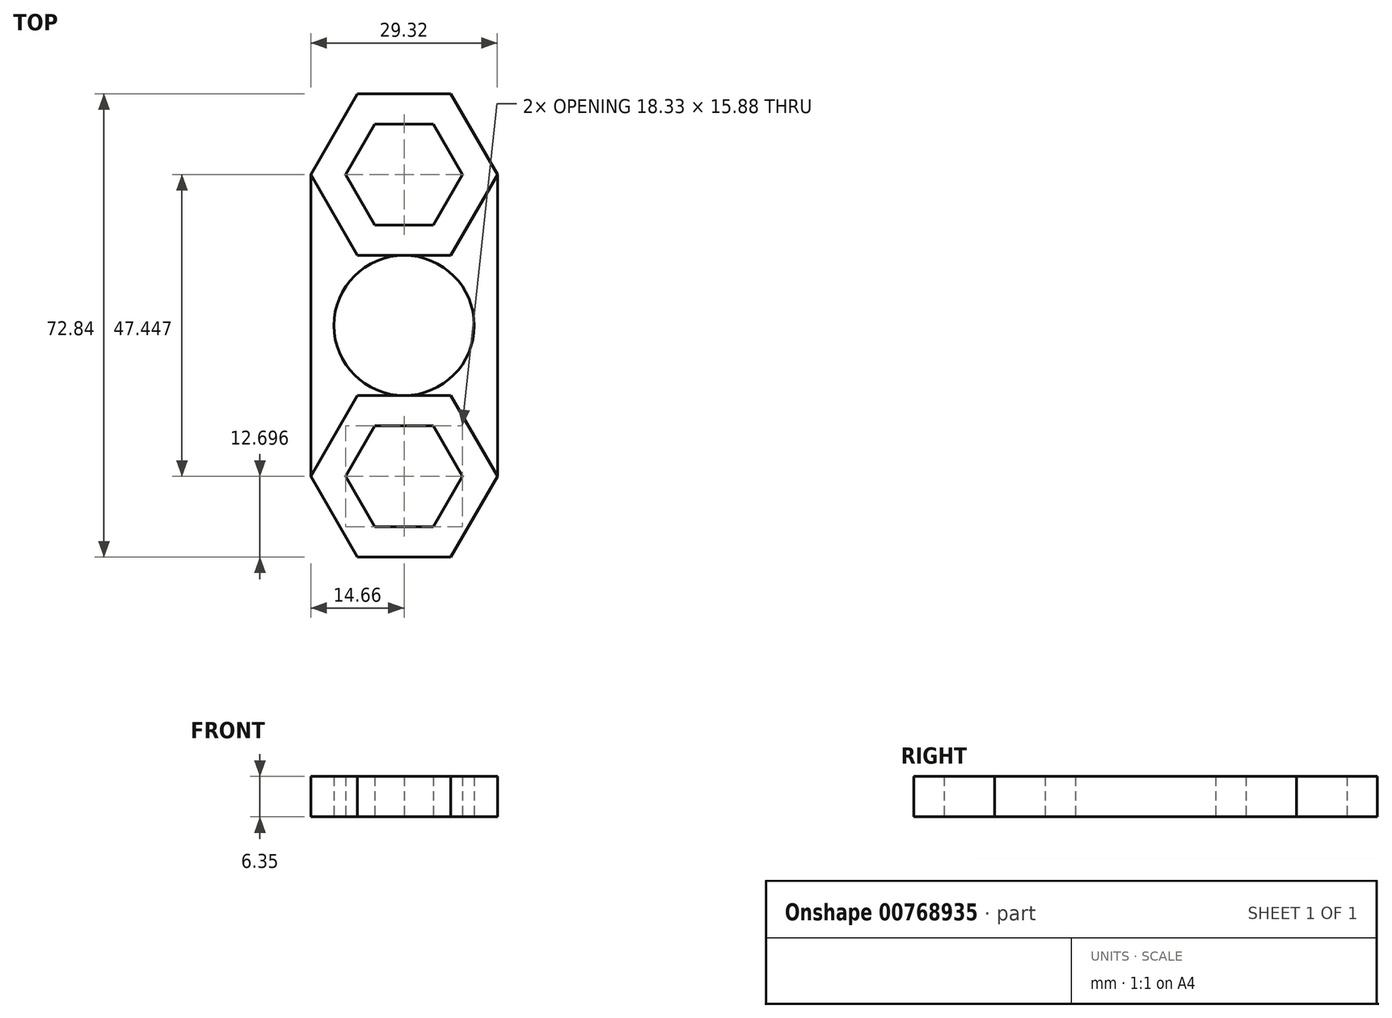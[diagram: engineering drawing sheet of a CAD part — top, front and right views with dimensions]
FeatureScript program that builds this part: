
annotation { "Feature Type Name" : "Feature", "Feature Type Description" : "" }
export const myFeature = defineFeature(function(context is Context, id is Id, definition is map)
    precondition{}
    {
        {
            var Q0;
            Q0=qCreatedBy(makeId("Top.planeOp"),FACE);
            var sketch = newSketch(context, id + "F0", { "sketchPlane" : qUnion([Q0])});
            skCircle(sketch, "E0", {"center": v(0, 0) * mm, "radius": 11.02 * mm});
            skCircle(sketch, "E1.cCircle", {"center": v(0, 23.72) * mm, "radius": 7.94 * mm, "construction": true});
            skLineSegment(sketch, "E1.0", {"start": v(4.58, 15.79) * mm, "end": v(-4.58, 15.79) * mm});
            skLineSegment(sketch, "E1.1", {"start": v(-4.58, 15.79) * mm, "end": v(-9.17, 23.72) * mm});
            skLineSegment(sketch, "E1.2", {"start": v(-9.17, 23.72) * mm, "end": v(-4.58, 31.66) * mm});
            skLineSegment(sketch, "E1.3", {"start": v(-4.58, 31.66) * mm, "end": v(4.58, 31.66) * mm});
            skLineSegment(sketch, "E1.4", {"start": v(4.58, 31.66) * mm, "end": v(9.17, 23.72) * mm});
            skLineSegment(sketch, "E1.5", {"start": v(9.17, 23.72) * mm, "end": v(4.58, 15.79) * mm});
            skPoint(sketch, "E1.0.midPoint", {"position": v(0, 15.79) * mm});
            skCircle(sketch, "E2.cCircle", {"center": v(0, 23.72) * mm, "radius": 12.7 * mm, "construction": true});
            skLineSegment(sketch, "E2.0", {"start": v(7.33, 11.02) * mm, "end": v(-7.33, 11.02) * mm});
            skLineSegment(sketch, "E2.1", {"start": v(-7.33, 11.02) * mm, "end": v(-14.66, 23.72) * mm});
            skLineSegment(sketch, "E2.2", {"start": v(-14.66, 23.72) * mm, "end": v(-7.33, 36.42) * mm});
            skLineSegment(sketch, "E2.3", {"start": v(-7.33, 36.42) * mm, "end": v(7.33, 36.42) * mm});
            skLineSegment(sketch, "E2.4", {"start": v(7.33, 36.42) * mm, "end": v(14.66, 23.72) * mm});
            skLineSegment(sketch, "E2.5", {"start": v(14.66, 23.72) * mm, "end": v(7.33, 11.02) * mm});
            skPoint(sketch, "E2.0.midPoint", {"position": v(0, 11.02) * mm});
            skLineSegment(sketch, "E3.1.0", {"start": v(-7.33, -36.42) * mm, "end": v(-14.66, -23.72) * mm});
            skPoint(sketch, "E3.1.1", {"position": v(0, -15.79) * mm});
            skCircle(sketch, "E3.1.2", {"center": v(0, -23.72) * mm, "radius": 7.94 * mm, "construction": true});
            skLineSegment(sketch, "E3.1.3", {"start": v(7.33, -36.42) * mm, "end": v(-7.33, -36.42) * mm});
            skLineSegment(sketch, "E3.1.4", {"start": v(14.66, -23.72) * mm, "end": v(7.33, -36.42) * mm});
            skLineSegment(sketch, "E3.1.5", {"start": v(9.17, -23.72) * mm, "end": v(4.58, -31.66) * mm});
            skLineSegment(sketch, "E3.1.6", {"start": v(4.58, -31.66) * mm, "end": v(-4.58, -31.66) * mm});
            skLineSegment(sketch, "E3.1.7", {"start": v(-4.58, -31.66) * mm, "end": v(-9.17, -23.72) * mm});
            skLineSegment(sketch, "E3.1.8", {"start": v(-9.17, -23.72) * mm, "end": v(-4.58, -15.79) * mm});
            skLineSegment(sketch, "E3.1.9", {"start": v(-4.58, -15.79) * mm, "end": v(4.58, -15.79) * mm});
            skLineSegment(sketch, "E3.1.10", {"start": v(4.58, -15.79) * mm, "end": v(9.17, -23.72) * mm});
            skLineSegment(sketch, "E3.1.11", {"start": v(-14.66, -23.72) * mm, "end": v(-7.33, -11.02) * mm});
            skLineSegment(sketch, "E3.1.12", {"start": v(7.33, -11.02) * mm, "end": v(14.66, -23.72) * mm});
            skLineSegment(sketch, "E3.1.13", {"start": v(-7.33, -11.02) * mm, "end": v(7.33, -11.02) * mm});
            skSolve(sketch);
        }
        {
            var Q0;
            Q0=qCreatedBy(makeId("Top.planeOp"),FACE);
            var sketch = newSketch(context, id + "F1", { "sketchPlane" : qUnion([Q0])});
            skLineSegment(sketch, "E4.0.0", {"start": v(9.17, -23.72) * mm, "end": v(4.58, -15.79) * mm});
            skLineSegment(sketch, "E4.0.1", {"start": v(4.58, -15.79) * mm, "end": v(-4.58, -15.79) * mm});
            skLineSegment(sketch, "E4.0.2", {"start": v(-4.58, -15.79) * mm, "end": v(-9.17, -23.72) * mm});
            skLineSegment(sketch, "E4.0.3", {"start": v(-9.17, -23.72) * mm, "end": v(-4.58, -31.66) * mm});
            skLineSegment(sketch, "E4.0.4", {"start": v(-4.58, -31.66) * mm, "end": v(4.58, -31.66) * mm});
            skLineSegment(sketch, "E4.0.5", {"start": v(4.58, -31.66) * mm, "end": v(9.17, -23.72) * mm});
            skLineSegment(sketch, "E5.0", {"start": v(9.17, 23.72) * mm, "end": v(4.58, 15.79) * mm});
            skCircle(sketch, "E5.1", {"center": v(0, 23.72) * mm, "radius": 12.7 * mm});
            skLineSegment(sketch, "E5.2", {"start": v(14.66, -23.72) * mm, "end": v(7.33, -36.42) * mm});
            skLineSegment(sketch, "E5.3", {"start": v(-14.66, -23.72) * mm, "end": v(-7.33, -11.02) * mm});
            skLineSegment(sketch, "E5.4", {"start": v(4.58, 31.66) * mm, "end": v(9.17, 23.72) * mm});
            skLineSegment(sketch, "E5.5", {"start": v(7.33, -36.42) * mm, "end": v(-7.33, -36.42) * mm});
            skLineSegment(sketch, "E5.6", {"start": v(-4.58, 31.66) * mm, "end": v(4.58, 31.66) * mm});
            skLineSegment(sketch, "E5.7", {"start": v(-9.17, 23.72) * mm, "end": v(-4.58, 31.66) * mm});
            skLineSegment(sketch, "E5.8", {"start": v(-4.58, 15.79) * mm, "end": v(-9.17, 23.72) * mm});
            skLineSegment(sketch, "E5.9", {"start": v(4.58, 15.79) * mm, "end": v(-4.58, 15.79) * mm});
            skCircle(sketch, "E5.10", {"center": v(0, 23.72) * mm, "radius": 7.94 * mm});
            skCircle(sketch, "E5.11", {"center": v(0, 0) * mm, "radius": 11.02 * mm});
            skLineSegment(sketch, "E5.12", {"start": v(-7.33, -36.42) * mm, "end": v(-14.66, -23.72) * mm});
            skLineSegment(sketch, "E5.13", {"start": v(14.66, 23.72) * mm, "end": v(7.33, 11.02) * mm});
            skLineSegment(sketch, "E5.14", {"start": v(7.33, 36.42) * mm, "end": v(14.66, 23.72) * mm});
            skLineSegment(sketch, "E5.15", {"start": v(-7.33, -11.02) * mm, "end": v(7.33, -11.02) * mm});
            skLineSegment(sketch, "E5.16", {"start": v(-7.33, 36.42) * mm, "end": v(7.33, 36.42) * mm});
            skLineSegment(sketch, "E5.17", {"start": v(-14.66, 23.72) * mm, "end": v(-7.33, 36.42) * mm});
            skLineSegment(sketch, "E5.18", {"start": v(-7.33, 11.02) * mm, "end": v(-14.66, 23.72) * mm});
            skLineSegment(sketch, "E5.19", {"start": v(7.33, -11.02) * mm, "end": v(14.66, -23.72) * mm});
            skLineSegment(sketch, "E5.20", {"start": v(7.33, 11.02) * mm, "end": v(-7.33, 11.02) * mm});
            skLineSegment(sketch, "E5.21", {"start": v(-9.17, -23.72) * mm, "end": v(-4.58, -15.79) * mm});
            skLineSegment(sketch, "E5.22", {"start": v(-4.58, -31.66) * mm, "end": v(-9.17, -23.72) * mm});
            skLineSegment(sketch, "E5.23", {"start": v(4.58, -15.79) * mm, "end": v(9.17, -23.72) * mm});
            skCircle(sketch, "E5.24", {"center": v(0, -23.72) * mm, "radius": 7.94 * mm});
            skLineSegment(sketch, "E5.25", {"start": v(4.58, -31.66) * mm, "end": v(-4.58, -31.66) * mm});
            skLineSegment(sketch, "E5.26", {"start": v(-4.58, -15.79) * mm, "end": v(4.58, -15.79) * mm});
            skLineSegment(sketch, "E5.27", {"start": v(9.17, -23.72) * mm, "end": v(4.58, -31.66) * mm});
            skLineSegment(sketch, "E6", {"start": v(-14.66, 23.72) * mm, "end": v(-14.66, -23.72) * mm});
            skLineSegment(sketch, "E7", {"start": v(14.66, 23.72) * mm, "end": v(14.66, -23.72) * mm});
            skSolve(sketch);
        }
        {
            var Q0;
            Q0=makeQuery(id+"F0.imprint","IMPRINT",FACE,{"disambiguationData":[TD([[makeQuery(id+"F0.imprint","IMPRINT",EDGE,{"derivedFrom":sQuery(id+"F0.wireOp",EDGE,"E1.0")}),1.0]])]});
            var Q1;
            {var subQ9=sQuery(id+"F1.wireOp",EDGE,"E5.3");Q1=makeQuery(id+"F1.imprint","IMPRINT",FACE,{"disambiguationData":[TD([[makeQuery(id+"F1.imprint","IMPRINT",EDGE,{"derivedFrom":subQ9}),1.0]])]});}
            var Q2;
            {var subQ5=sQuery(id+"F1.wireOp",EDGE,"E5.19");Q2=makeQuery(id+"F1.imprint","IMPRINT",FACE,{"disambiguationData":[TD([[makeQuery(id+"F1.imprint","IMPRINT",EDGE,{"derivedFrom":subQ5}),1.0]])]});}
            var Q3;
            Q3=makeQuery(id+"F0.imprint","IMPRINT",FACE,{"disambiguationData":[TD([[makeQuery(id+"F0.imprint","IMPRINT",EDGE,{"derivedFrom":sQuery(id+"F0.wireOp",EDGE,"E3.1.0")}),-1.0]])]});
            extrude(context, id + "F2", {"entities" : qUnion([Q0, Q1, Q2, Q3]), "depth" : 6.35 * mm, "offsetDistance" : 25.4 * mm});
        }
    });
